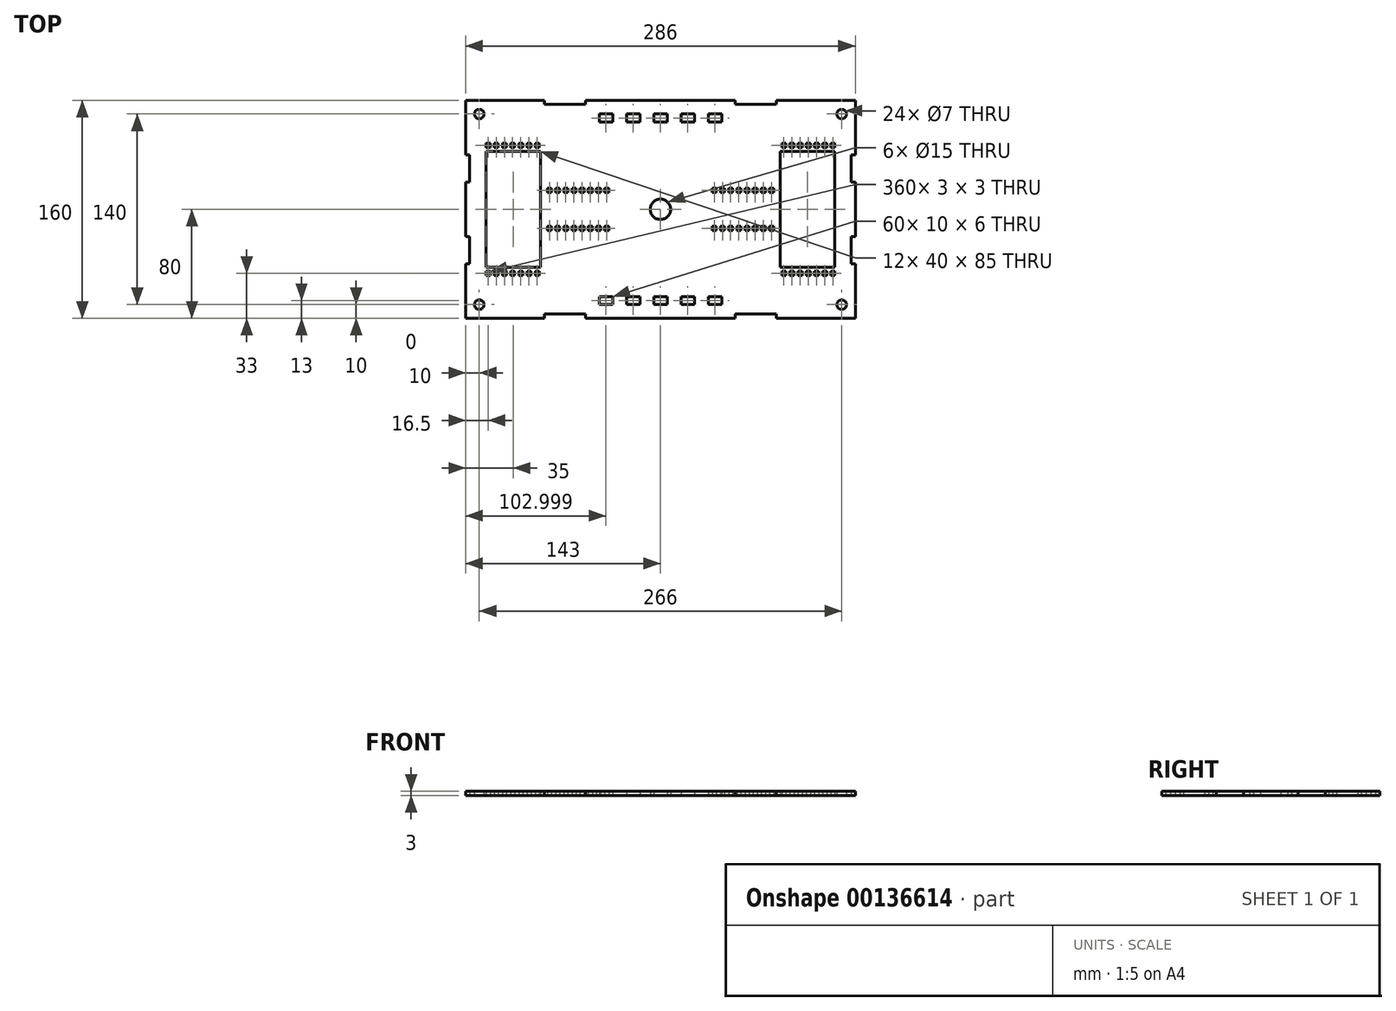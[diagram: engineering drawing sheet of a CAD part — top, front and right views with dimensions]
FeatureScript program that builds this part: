
annotation { "Feature Type Name" : "Feature", "Feature Type Description" : "" }
export const myFeature = defineFeature(function(context is Context, id is Id, definition is map)
    precondition{}
    {
        {
            var Q0;
            Q0=qCreatedBy(makeId("Top.planeOp"),FACE);
            var sketch = newSketch(context, id + "F0", { "sketchPlane" : qUnion([Q0])});
            skLineSegment(sketch, "E0.bottom", {"start": v(143, 80) * mm, "end": v(85, 80) * mm});
            skLineSegment(sketch, "E0.top", {"start": v(143, -80) * mm, "end": v(85, -80) * mm});
            skLineSegment(sketch, "E0.left", {"start": v(143, 80) * mm, "end": v(143, 40) * mm});
            skLineSegment(sketch, "E0.right", {"start": v(-143, 80) * mm, "end": v(-143, 40) * mm});
            skPoint(sketch, "E0.middle", {"position": v(0, 0) * mm});
            skCircle(sketch, "E1", {"center": v(0, 0) * mm, "radius": 7.5 * mm});
            skLineSegment(sketch, "E2", {"start": v(143, 0) * mm, "end": v(128, 0) * mm, "construction": true});
            skLineSegment(sketch, "E3", {"start": v(-70, 0) * mm, "end": v(-65, 0) * mm, "construction": true});
            skLineSegment(sketch, "E4", {"start": v(-65, 0) * mm, "end": v(-65, 12.5) * mm, "construction": true});
            skLineSegment(sketch, "E5", {"start": v(-65, 0) * mm, "end": v(-65, -12.5) * mm, "construction": true});
            skLineSegment(sketch, "E6", {"start": v(-65, 12.5) * mm, "end": v(-62, 12.5) * mm});
            skLineSegment(sketch, "E7", {"start": v(-62, 12.5) * mm, "end": v(-62, 15.5) * mm});
            skLineSegment(sketch, "E8", {"start": v(-62, 15.5) * mm, "end": v(-65, 15.5) * mm});
            skLineSegment(sketch, "E9", {"start": v(-65, 15.5) * mm, "end": v(-65, 12.5) * mm});
            skLineSegment(sketch, "E10", {"start": v(-62, 12.5) * mm, "end": v(-59, 12.5) * mm, "construction": true});
            skLineSegment(sketch, "E11", {"start": v(-59, 12.5) * mm, "end": v(-56, 12.5) * mm, "construction": true});
            skLineSegment(sketch, "E12", {"start": v(-56, 12.5) * mm, "end": v(-53, 12.5) * mm, "construction": true});
            skLineSegment(sketch, "E13", {"start": v(-53, 12.5) * mm, "end": v(-50, 12.5) * mm, "construction": true});
            skLineSegment(sketch, "E14", {"start": v(-50, 12.5) * mm, "end": v(-47, 12.5) * mm, "construction": true});
            skLineSegment(sketch, "E15", {"start": v(-47, 12.5) * mm, "end": v(-44, 12.5) * mm, "construction": true});
            skLineSegment(sketch, "E16", {"start": v(-44, 12.5) * mm, "end": v(-41, 12.5) * mm, "construction": true});
            skLineSegment(sketch, "E17", {"start": v(-41, 12.5) * mm, "end": v(-38, 12.5) * mm, "construction": true});
            skLineSegment(sketch, "E18.bottom", {"start": v(-59, 12.5) * mm, "end": v(-56, 12.5) * mm});
            skLineSegment(sketch, "E18.top", {"start": v(-59, 15.5) * mm, "end": v(-56, 15.5) * mm});
            skLineSegment(sketch, "E18.left", {"start": v(-59, 12.5) * mm, "end": v(-59, 15.5) * mm});
            skLineSegment(sketch, "E18.right", {"start": v(-56, 12.5) * mm, "end": v(-56, 15.5) * mm});
            skLineSegment(sketch, "E19.bottom", {"start": v(-53, 12.5) * mm, "end": v(-50, 12.5) * mm});
            skLineSegment(sketch, "E19.top", {"start": v(-53, 15.5) * mm, "end": v(-50, 15.5) * mm});
            skLineSegment(sketch, "E19.left", {"start": v(-53, 12.5) * mm, "end": v(-53, 15.5) * mm});
            skLineSegment(sketch, "E19.right", {"start": v(-50, 12.5) * mm, "end": v(-50, 15.5) * mm});
            skLineSegment(sketch, "E20.bottom", {"start": v(-47, 12.5) * mm, "end": v(-44, 12.5) * mm});
            skLineSegment(sketch, "E20.top", {"start": v(-47, 15.5) * mm, "end": v(-44, 15.5) * mm});
            skLineSegment(sketch, "E20.left", {"start": v(-47, 12.5) * mm, "end": v(-47, 15.5) * mm});
            skLineSegment(sketch, "E20.right", {"start": v(-44, 12.5) * mm, "end": v(-44, 15.5) * mm});
            skLineSegment(sketch, "E21.bottom", {"start": v(-41, 12.5) * mm, "end": v(-38, 12.5) * mm});
            skLineSegment(sketch, "E21.top", {"start": v(-41, 15.5) * mm, "end": v(-38, 15.5) * mm});
            skLineSegment(sketch, "E21.left", {"start": v(-41, 12.5) * mm, "end": v(-41, 15.5) * mm});
            skLineSegment(sketch, "E21.right", {"start": v(-38, 12.5) * mm, "end": v(-38, 15.5) * mm});
            skLineSegment(sketch, "E22", {"start": v(-65, 12.5) * mm, "end": v(-68, 12.5) * mm, "construction": true});
            skLineSegment(sketch, "E23", {"start": v(-68, 12.5) * mm, "end": v(-71, 12.5) * mm, "construction": true});
            skLineSegment(sketch, "E24", {"start": v(-71, 12.5) * mm, "end": v(-74, 12.5) * mm, "construction": true});
            skLineSegment(sketch, "E25", {"start": v(-74, 12.5) * mm, "end": v(-77, 12.5) * mm, "construction": true});
            skLineSegment(sketch, "E26", {"start": v(-77, 12.5) * mm, "end": v(-80, 12.5) * mm, "construction": true});
            skLineSegment(sketch, "E27", {"start": v(-80, 12.5) * mm, "end": v(-83, 12.5) * mm, "construction": true});
            skLineSegment(sketch, "E28.bottom", {"start": v(-71, 12.5) * mm, "end": v(-68, 12.5) * mm});
            skLineSegment(sketch, "E28.top", {"start": v(-71, 15.5) * mm, "end": v(-68, 15.5) * mm});
            skLineSegment(sketch, "E28.left", {"start": v(-71, 12.5) * mm, "end": v(-71, 15.5) * mm});
            skLineSegment(sketch, "E28.right", {"start": v(-68, 12.5) * mm, "end": v(-68, 15.5) * mm});
            skLineSegment(sketch, "E29.bottom", {"start": v(-77, 12.5) * mm, "end": v(-74, 12.5) * mm});
            skLineSegment(sketch, "E29.top", {"start": v(-77, 15.5) * mm, "end": v(-74, 15.5) * mm});
            skLineSegment(sketch, "E29.left", {"start": v(-77, 12.5) * mm, "end": v(-77, 15.5) * mm});
            skLineSegment(sketch, "E29.right", {"start": v(-74, 12.5) * mm, "end": v(-74, 15.5) * mm});
            skPoint(sketch, "E30.oppositeSnap0", {"position": v(-75.5, 15.5) * mm});
            skLineSegment(sketch, "E30.bottom", {"start": v(-83, 12.5) * mm, "end": v(-80, 12.5) * mm});
            skLineSegment(sketch, "E30.top", {"start": v(-83, 15.5) * mm, "end": v(-80, 15.5) * mm});
            skLineSegment(sketch, "E30.left", {"start": v(-83, 12.5) * mm, "end": v(-83, 15.5) * mm});
            skLineSegment(sketch, "E30.right", {"start": v(-80, 12.5) * mm, "end": v(-80, 15.5) * mm});
            skLineSegment(sketch, "E31.MirrorCS", {"start": v(-77, -12.5) * mm, "end": v(-74, -12.5) * mm});
            skLineSegment(sketch, "E32.MirrorCS", {"start": v(-71, -12.5) * mm, "end": v(-68, -12.5) * mm});
            skLineSegment(sketch, "E33.MirrorCS", {"start": v(-74, -12.5) * mm, "end": v(-77, -12.5) * mm, "construction": true});
            skLineSegment(sketch, "E34.MirrorCS", {"start": v(-77, -12.5) * mm, "end": v(-80, -12.5) * mm, "construction": true});
            skLineSegment(sketch, "E35.MirrorCS", {"start": v(-65, -12.5) * mm, "end": v(-68, -12.5) * mm, "construction": true});
            skLineSegment(sketch, "E36.MirrorCS", {"start": v(-68, -12.5) * mm, "end": v(-71, -12.5) * mm, "construction": true});
            skLineSegment(sketch, "E37.MirrorCS", {"start": v(-83, -12.5) * mm, "end": v(-80, -12.5) * mm});
            skLineSegment(sketch, "E38.MirrorCS", {"start": v(-71, -12.5) * mm, "end": v(-74, -12.5) * mm, "construction": true});
            skLineSegment(sketch, "E39.MirrorCS", {"start": v(-74, -12.5) * mm, "end": v(-74, -15.5) * mm});
            skLineSegment(sketch, "E40.MirrorCS", {"start": v(-80, -12.5) * mm, "end": v(-83, -12.5) * mm, "construction": true});
            skLineSegment(sketch, "E41.MirrorCS", {"start": v(-83, -12.5) * mm, "end": v(-83, -15.5) * mm});
            skLineSegment(sketch, "E42.MirrorCS", {"start": v(-71, -12.5) * mm, "end": v(-71, -15.5) * mm});
            skLineSegment(sketch, "E43.MirrorCS", {"start": v(-83, -15.5) * mm, "end": v(-80, -15.5) * mm});
            skLineSegment(sketch, "E44.MirrorCS", {"start": v(-77, -12.5) * mm, "end": v(-77, -15.5) * mm});
            skLineSegment(sketch, "E45.MirrorCS", {"start": v(-80, -12.5) * mm, "end": v(-80, -15.5) * mm});
            skLineSegment(sketch, "E46.MirrorCS", {"start": v(-68, -12.5) * mm, "end": v(-68, -15.5) * mm});
            skLineSegment(sketch, "E47.MirrorCS", {"start": v(-71, -15.5) * mm, "end": v(-68, -15.5) * mm});
            skLineSegment(sketch, "E48.MirrorCS", {"start": v(-77, -15.5) * mm, "end": v(-74, -15.5) * mm});
            skPoint(sketch, "E49.MirrorP", {"position": v(-70.5, -15.5) * mm});
            skLineSegment(sketch, "E50", {"start": v(-83, 12.5) * mm, "end": v(-83, -12.5) * mm, "construction": true});
            skLineSegment(sketch, "E51", {"start": v(-83, 0) * mm, "end": v(-88, 0) * mm, "construction": true});
            skLineSegment(sketch, "E52", {"start": v(-88, 0) * mm, "end": v(-108, 0) * mm, "construction": true});
            skLineSegment(sketch, "E53.bottom", {"start": v(-88, 42.5) * mm, "end": v(-128, 42.5) * mm});
            skLineSegment(sketch, "E53.top", {"start": v(-88, -42.5) * mm, "end": v(-128, -42.5) * mm});
            skLineSegment(sketch, "E53.left", {"start": v(-88, 42.5) * mm, "end": v(-88, -42.5) * mm});
            skLineSegment(sketch, "E53.right", {"start": v(-128, 42.5) * mm, "end": v(-128, -42.5) * mm});
            skPoint(sketch, "E53.middle", {"position": v(-108, 0) * mm});
            skLineSegment(sketch, "E54", {"start": v(0, 80) * mm, "end": v(0, 70) * mm, "construction": true});
            skLineSegment(sketch, "E55", {"start": v(-128, 42.5) * mm, "end": v(-128, 45.5) * mm, "construction": true});
            skLineSegment(sketch, "E56", {"start": v(-128, 45.5) * mm, "end": v(-125, 45.5) * mm, "construction": true});
            skLineSegment(sketch, "E57", {"start": v(-125, 45.5) * mm, "end": v(-122, 45.5) * mm, "construction": true});
            skPoint(sketch, "E57.endSnap0", {"position": v(-126.5, 45.5) * mm});
            skLineSegment(sketch, "E58", {"start": v(-122, 45.5) * mm, "end": v(-119, 45.5) * mm, "construction": true});
            skLineSegment(sketch, "E59", {"start": v(-119, 45.5) * mm, "end": v(-116, 45.5) * mm, "construction": true});
            skLineSegment(sketch, "E60", {"start": v(-116, 45.5) * mm, "end": v(-113, 45.5) * mm, "construction": true});
            skLineSegment(sketch, "E61", {"start": v(-113, 45.5) * mm, "end": v(-110, 45.5) * mm, "construction": true});
            skLineSegment(sketch, "E62", {"start": v(-110, 45.5) * mm, "end": v(-107, 45.5) * mm, "construction": true});
            skLineSegment(sketch, "E63", {"start": v(-107, 45.5) * mm, "end": v(-104, 45.5) * mm, "construction": true});
            skLineSegment(sketch, "E64", {"start": v(-104, 45.5) * mm, "end": v(-101, 45.5) * mm, "construction": true});
            skLineSegment(sketch, "E65", {"start": v(-101, 45.5) * mm, "end": v(-98, 45.5) * mm, "construction": true});
            skLineSegment(sketch, "E66", {"start": v(-98, 45.5) * mm, "end": v(-95, 45.5) * mm, "construction": true});
            skLineSegment(sketch, "E67", {"start": v(-95, 45.5) * mm, "end": v(-92, 45.5) * mm, "construction": true});
            skLineSegment(sketch, "E68", {"start": v(-92, 45.5) * mm, "end": v(-89, 45.5) * mm, "construction": true});
            skLineSegment(sketch, "E69.bottom", {"start": v(-128, 45.5) * mm, "end": v(-125, 45.5) * mm});
            skLineSegment(sketch, "E69.top", {"start": v(-128, 48.5) * mm, "end": v(-125, 48.5) * mm});
            skLineSegment(sketch, "E69.left", {"start": v(-128, 45.5) * mm, "end": v(-128, 48.5) * mm});
            skLineSegment(sketch, "E69.right", {"start": v(-125, 45.5) * mm, "end": v(-125, 48.5) * mm});
            skLineSegment(sketch, "E70.bottom", {"start": v(-122, 45.5) * mm, "end": v(-119, 45.5) * mm});
            skLineSegment(sketch, "E70.top", {"start": v(-122, 48.5) * mm, "end": v(-119, 48.5) * mm});
            skLineSegment(sketch, "E70.left", {"start": v(-122, 45.5) * mm, "end": v(-122, 48.5) * mm});
            skLineSegment(sketch, "E70.right", {"start": v(-119, 45.5) * mm, "end": v(-119, 48.5) * mm});
            skLineSegment(sketch, "E71.bottom", {"start": v(-116, 45.5) * mm, "end": v(-113, 45.5) * mm});
            skLineSegment(sketch, "E71.top", {"start": v(-116, 48.5) * mm, "end": v(-113, 48.5) * mm});
            skLineSegment(sketch, "E71.left", {"start": v(-116, 45.5) * mm, "end": v(-116, 48.5) * mm});
            skLineSegment(sketch, "E71.right", {"start": v(-113, 45.5) * mm, "end": v(-113, 48.5) * mm});
            skLineSegment(sketch, "E72.bottom", {"start": v(-110, 45.5) * mm, "end": v(-107, 45.5) * mm});
            skLineSegment(sketch, "E72.top", {"start": v(-110, 48.5) * mm, "end": v(-107, 48.5) * mm});
            skLineSegment(sketch, "E72.left", {"start": v(-110, 45.5) * mm, "end": v(-110, 48.5) * mm});
            skLineSegment(sketch, "E72.right", {"start": v(-107, 45.5) * mm, "end": v(-107, 48.5) * mm});
            skLineSegment(sketch, "E73.bottom", {"start": v(-104, 45.5) * mm, "end": v(-101, 45.5) * mm});
            skLineSegment(sketch, "E73.top", {"start": v(-104, 48.5) * mm, "end": v(-101, 48.5) * mm});
            skLineSegment(sketch, "E73.left", {"start": v(-104, 45.5) * mm, "end": v(-104, 48.5) * mm});
            skLineSegment(sketch, "E73.right", {"start": v(-101, 45.5) * mm, "end": v(-101, 48.5) * mm});
            skLineSegment(sketch, "E74.bottom", {"start": v(-98, 45.5) * mm, "end": v(-95, 45.5) * mm});
            skLineSegment(sketch, "E74.top", {"start": v(-98, 48.5) * mm, "end": v(-95, 48.5) * mm});
            skLineSegment(sketch, "E74.left", {"start": v(-98, 45.5) * mm, "end": v(-98, 48.5) * mm});
            skLineSegment(sketch, "E74.right", {"start": v(-95, 45.5) * mm, "end": v(-95, 48.5) * mm});
            skLineSegment(sketch, "E75.bottom", {"start": v(-92, 45.5) * mm, "end": v(-89, 45.5) * mm});
            skLineSegment(sketch, "E75.top", {"start": v(-92, 48.5) * mm, "end": v(-89, 48.5) * mm});
            skLineSegment(sketch, "E75.left", {"start": v(-92, 45.5) * mm, "end": v(-92, 48.5) * mm});
            skLineSegment(sketch, "E75.right", {"start": v(-89, 45.5) * mm, "end": v(-89, 48.5) * mm});
            skLineSegment(sketch, "E76", {"start": v(-143, -80) * mm, "end": v(-133, -80) * mm, "construction": true});
            skLineSegment(sketch, "E77", {"start": v(-133, -80) * mm, "end": v(-133, -70) * mm, "construction": true});
            skCircle(sketch, "E78", {"center": v(-133, -70) * mm, "radius": 3.5 * mm});
            skCircle(sketch, "E79.MirrorC", {"center": v(133, -70) * mm, "radius": 3.5 * mm});
            skCircle(sketch, "E80.MirrorC", {"center": v(133, 70) * mm, "radius": 3.5 * mm});
            skCircle(sketch, "E81.MirrorC", {"center": v(-133, 70) * mm, "radius": 3.5 * mm});
            skLineSegment(sketch, "E82", {"start": v(0, -70) * mm, "end": v(45, -70) * mm, "construction": true});
            skLineSegment(sketch, "E83", {"start": v(0, -70) * mm, "end": v(-22.5, -70) * mm, "construction": true});
            skLineSegment(sketch, "E84", {"start": v(-45, -70) * mm, "end": v(-45, -64) * mm});
            skLineSegment(sketch, "E85", {"start": v(-45, -64) * mm, "end": v(-35, -64) * mm});
            skLineSegment(sketch, "E86", {"start": v(-35, -64) * mm, "end": v(-35, -70) * mm});
            skLineSegment(sketch, "E87", {"start": v(-35, -70) * mm, "end": v(-45, -70) * mm});
            skLineSegment(sketch, "E88.trimOffspring", {"start": v(-35, -70) * mm, "end": v(-45, -70) * mm, "construction": true});
            skLineSegment(sketch, "E89", {"start": v(-35, -70) * mm, "end": v(-25, -70) * mm, "construction": true});
            skLineSegment(sketch, "E90", {"start": v(-25, -70) * mm, "end": v(-11.25, -70) * mm, "construction": true});
            skLineSegment(sketch, "E91", {"start": v(-25, -70) * mm, "end": v(-15, -70) * mm, "construction": true});
            skLineSegment(sketch, "E92", {"start": v(-15, -70) * mm, "end": v(-5, -70) * mm, "construction": true});
            skLineSegment(sketch, "E93", {"start": v(-5, -70) * mm, "end": v(5, -70) * mm, "construction": true});
            skLineSegment(sketch, "E94", {"start": v(5, -70) * mm, "end": v(15, -70) * mm, "construction": true});
            skLineSegment(sketch, "E95", {"start": v(15, -70) * mm, "end": v(25, -70) * mm, "construction": true});
            skLineSegment(sketch, "E96", {"start": v(25, -70) * mm, "end": v(35, -70) * mm, "construction": true});
            skLineSegment(sketch, "E97.bottom", {"start": v(-25, -70) * mm, "end": v(-15, -70) * mm});
            skLineSegment(sketch, "E97.top", {"start": v(-25, -64) * mm, "end": v(-15, -64) * mm});
            skLineSegment(sketch, "E97.left", {"start": v(-25, -70) * mm, "end": v(-25, -64) * mm});
            skLineSegment(sketch, "E97.right", {"start": v(-15, -70) * mm, "end": v(-15, -64) * mm});
            skLineSegment(sketch, "E98.bottom", {"start": v(-5, -70) * mm, "end": v(5, -70) * mm});
            skLineSegment(sketch, "E98.top", {"start": v(-5, -64) * mm, "end": v(5, -64) * mm});
            skLineSegment(sketch, "E98.left", {"start": v(-5, -70) * mm, "end": v(-5, -64) * mm});
            skLineSegment(sketch, "E98.right", {"start": v(5, -70) * mm, "end": v(5, -64) * mm});
            skLineSegment(sketch, "E99.bottom", {"start": v(15, -70) * mm, "end": v(25, -70) * mm});
            skLineSegment(sketch, "E99.top", {"start": v(15, -64) * mm, "end": v(25, -64) * mm});
            skLineSegment(sketch, "E99.left", {"start": v(15, -70) * mm, "end": v(15, -64) * mm});
            skLineSegment(sketch, "E99.right", {"start": v(25, -70) * mm, "end": v(25, -64) * mm});
            skLineSegment(sketch, "E100.bottom", {"start": v(35, -70) * mm, "end": v(45, -70) * mm});
            skLineSegment(sketch, "E100.top", {"start": v(35, -64) * mm, "end": v(45, -64) * mm});
            skLineSegment(sketch, "E100.left", {"start": v(35, -70) * mm, "end": v(35, -64) * mm});
            skLineSegment(sketch, "E100.right", {"start": v(45, -70) * mm, "end": v(45, -64) * mm});
            skLineSegment(sketch, "E101.MirrorCS", {"start": v(77, 12.5) * mm, "end": v(74, 12.5) * mm});
            skLineSegment(sketch, "E102.MirrorCS", {"start": v(71, -12.5) * mm, "end": v(68, -12.5) * mm});
            skLineSegment(sketch, "E103.MirrorCS", {"start": v(71, 12.5) * mm, "end": v(71, 15.5) * mm});
            skLineSegment(sketch, "E104.MirrorCS", {"start": v(77, 15.5) * mm, "end": v(74, 15.5) * mm});
            skLineSegment(sketch, "E105.MirrorCS", {"start": v(77, 12.5) * mm, "end": v(77, 15.5) * mm});
            skLineSegment(sketch, "E106.MirrorCS", {"start": v(74, 12.5) * mm, "end": v(74, 15.5) * mm});
            skLineSegment(sketch, "E107.MirrorCS", {"start": v(71, 12.5) * mm, "end": v(74, 12.5) * mm, "construction": true});
            skLineSegment(sketch, "E108.MirrorCS", {"start": v(83, -12.5) * mm, "end": v(80, -12.5) * mm});
            skLineSegment(sketch, "E109.MirrorCS", {"start": v(74, 12.5) * mm, "end": v(77, 12.5) * mm, "construction": true});
            skLineSegment(sketch, "E110.MirrorCS", {"start": v(53, 12.5) * mm, "end": v(50, 12.5) * mm});
            skLineSegment(sketch, "E111.MirrorCS", {"start": v(53, 15.5) * mm, "end": v(50, 15.5) * mm});
            skLineSegment(sketch, "E112.MirrorCS", {"start": v(80, -12.5) * mm, "end": v(80, -15.5) * mm});
            skLineSegment(sketch, "E113.MirrorCS", {"start": v(47, 12.5) * mm, "end": v(44, 12.5) * mm});
            skLineSegment(sketch, "E114.MirrorCS", {"start": v(68, 12.5) * mm, "end": v(68, 15.5) * mm});
            skLineSegment(sketch, "E115.MirrorCS", {"start": v(77, -12.5) * mm, "end": v(80, -12.5) * mm, "construction": true});
            skLineSegment(sketch, "E116.MirrorCS", {"start": v(71, 12.5) * mm, "end": v(68, 12.5) * mm});
            skLineSegment(sketch, "E117.MirrorCS", {"start": v(53, 12.5) * mm, "end": v(53, 15.5) * mm});
            skLineSegment(sketch, "E118.MirrorCS", {"start": v(53, 12.5) * mm, "end": v(50, 12.5) * mm, "construction": true});
            skLineSegment(sketch, "E119.MirrorCS", {"start": v(80, -12.5) * mm, "end": v(83, -12.5) * mm, "construction": true});
            skLineSegment(sketch, "E120.MirrorCS", {"start": v(41, 12.5) * mm, "end": v(38, 12.5) * mm});
            skLineSegment(sketch, "E121.MirrorCS", {"start": v(83, -12.5) * mm, "end": v(83, -15.5) * mm});
            skLineSegment(sketch, "E122.MirrorCS", {"start": v(50, 12.5) * mm, "end": v(50, 15.5) * mm});
            skLineSegment(sketch, "E123.MirrorCS", {"start": v(71, -12.5) * mm, "end": v(71, -15.5) * mm});
            skLineSegment(sketch, "E124.MirrorCS", {"start": v(68, -12.5) * mm, "end": v(71, -12.5) * mm, "construction": true});
            skLineSegment(sketch, "E125.MirrorCS", {"start": v(77, -12.5) * mm, "end": v(74, -12.5) * mm});
            skLineSegment(sketch, "E126.MirrorCS", {"start": v(59, 12.5) * mm, "end": v(56, 12.5) * mm});
            skLineSegment(sketch, "E127.MirrorCS", {"start": v(65, 12.5) * mm, "end": v(68, 12.5) * mm, "construction": true});
            skLineSegment(sketch, "E128.MirrorCS", {"start": v(62, 12.5) * mm, "end": v(59, 12.5) * mm, "construction": true});
            skLineSegment(sketch, "E129.MirrorCS", {"start": v(56, 12.5) * mm, "end": v(53, 12.5) * mm, "construction": true});
            skLineSegment(sketch, "E130.MirrorCS", {"start": v(65, 12.5) * mm, "end": v(62, 12.5) * mm});
            skLineSegment(sketch, "E131.MirrorCS", {"start": v(62, 12.5) * mm, "end": v(62, 15.5) * mm});
            skLineSegment(sketch, "E132.MirrorCS", {"start": v(62, 15.5) * mm, "end": v(65, 15.5) * mm});
            skLineSegment(sketch, "E133.MirrorCS", {"start": v(65, 15.5) * mm, "end": v(65, 12.5) * mm});
            skLineSegment(sketch, "E134.MirrorCS", {"start": v(59, 12.5) * mm, "end": v(59, 15.5) * mm});
            skLineSegment(sketch, "E135.MirrorCS", {"start": v(71, -12.5) * mm, "end": v(74, -12.5) * mm, "construction": true});
            skLineSegment(sketch, "E136.MirrorCS", {"start": v(74, -12.5) * mm, "end": v(74, -15.5) * mm});
            skLineSegment(sketch, "E137.MirrorCS", {"start": v(47, 15.5) * mm, "end": v(44, 15.5) * mm});
            skLineSegment(sketch, "E138.MirrorCS", {"start": v(47, 12.5) * mm, "end": v(47, 15.5) * mm});
            skLineSegment(sketch, "E139.MirrorCS", {"start": v(68, -12.5) * mm, "end": v(68, -15.5) * mm});
            skLineSegment(sketch, "E140.MirrorCS", {"start": v(44, 12.5) * mm, "end": v(44, 15.5) * mm});
            skLineSegment(sketch, "E141.MirrorCS", {"start": v(50, 12.5) * mm, "end": v(47, 12.5) * mm, "construction": true});
            skLineSegment(sketch, "E142.MirrorCS", {"start": v(65, -12.5) * mm, "end": v(68, -12.5) * mm, "construction": true});
            skLineSegment(sketch, "E143.MirrorCS", {"start": v(47, 12.5) * mm, "end": v(44, 12.5) * mm, "construction": true});
            skLineSegment(sketch, "E144.MirrorCS", {"start": v(74, -12.5) * mm, "end": v(77, -12.5) * mm, "construction": true});
            skLineSegment(sketch, "E145.MirrorCS", {"start": v(71, 15.5) * mm, "end": v(68, 15.5) * mm});
            skLineSegment(sketch, "E146.MirrorCS", {"start": v(41, 15.5) * mm, "end": v(38, 15.5) * mm});
            skLineSegment(sketch, "E147.MirrorCS", {"start": v(44, 12.5) * mm, "end": v(41, 12.5) * mm, "construction": true});
            skLineSegment(sketch, "E148.MirrorCS", {"start": v(83, 12.5) * mm, "end": v(80, 12.5) * mm});
            skLineSegment(sketch, "E149.MirrorCS", {"start": v(41, 12.5) * mm, "end": v(41, 15.5) * mm});
            skLineSegment(sketch, "E150.MirrorCS", {"start": v(41, 12.5) * mm, "end": v(38, 12.5) * mm, "construction": true});
            skLineSegment(sketch, "E151.MirrorCS", {"start": v(77, 12.5) * mm, "end": v(80, 12.5) * mm, "construction": true});
            skLineSegment(sketch, "E152.MirrorCS", {"start": v(59, 12.5) * mm, "end": v(56, 12.5) * mm, "construction": true});
            skLineSegment(sketch, "E153.MirrorCS", {"start": v(59, 15.5) * mm, "end": v(56, 15.5) * mm});
            skLineSegment(sketch, "E154.MirrorCS", {"start": v(68, 12.5) * mm, "end": v(71, 12.5) * mm, "construction": true});
            skLineSegment(sketch, "E155.MirrorCS", {"start": v(77, -12.5) * mm, "end": v(77, -15.5) * mm});
            skLineSegment(sketch, "E156.MirrorCS", {"start": v(56, 12.5) * mm, "end": v(56, 15.5) * mm});
            skLineSegment(sketch, "E157.MirrorCS", {"start": v(80, 12.5) * mm, "end": v(83, 12.5) * mm, "construction": true});
            skLineSegment(sketch, "E158.MirrorCS", {"start": v(83, 15.5) * mm, "end": v(80, 15.5) * mm});
            skLineSegment(sketch, "E159.MirrorCS", {"start": v(83, 12.5) * mm, "end": v(83, 15.5) * mm});
            skLineSegment(sketch, "E160.MirrorCS", {"start": v(80, 12.5) * mm, "end": v(80, 15.5) * mm});
            skLineSegment(sketch, "E161.MirrorCS", {"start": v(77, -15.5) * mm, "end": v(74, -15.5) * mm});
            skLineSegment(sketch, "E162.MirrorCS", {"start": v(38, 12.5) * mm, "end": v(38, 15.5) * mm});
            skLineSegment(sketch, "E163.MirrorCS", {"start": v(71, -15.5) * mm, "end": v(68, -15.5) * mm});
            skLineSegment(sketch, "E164.MirrorCS", {"start": v(83, -15.5) * mm, "end": v(80, -15.5) * mm});
            skLineSegment(sketch, "E165.MirrorCS", {"start": v(70, 0) * mm, "end": v(65, 0) * mm, "construction": true});
            skLineSegment(sketch, "E166.MirrorCS", {"start": v(65, 0) * mm, "end": v(65, 12.5) * mm, "construction": true});
            skLineSegment(sketch, "E167.MirrorCS", {"start": v(83, 0) * mm, "end": v(88, 0) * mm, "construction": true});
            skPoint(sketch, "E168.MirrorP", {"position": v(75.5, 15.5) * mm});
            skPoint(sketch, "E169.MirrorP", {"position": v(70.5, -15.5) * mm});
            skLineSegment(sketch, "E170.MirrorCS", {"start": v(83, 12.5) * mm, "end": v(83, -12.5) * mm, "construction": true});
            skLineSegment(sketch, "E171.MirrorCS", {"start": v(65, 0) * mm, "end": v(65, -12.5) * mm, "construction": true});
            skLineSegment(sketch, "E172.MirrorCS", {"start": v(104, 45.5) * mm, "end": v(101, 45.5) * mm});
            skLineSegment(sketch, "E173.MirrorCS", {"start": v(110, 45.5) * mm, "end": v(107, 45.5) * mm});
            skLineSegment(sketch, "E174.MirrorCS", {"start": v(98, 45.5) * mm, "end": v(98, 48.5) * mm});
            skLineSegment(sketch, "E175.MirrorCS", {"start": v(104, 45.5) * mm, "end": v(101, 45.5) * mm, "construction": true});
            skLineSegment(sketch, "E176.MirrorCS", {"start": v(113, 45.5) * mm, "end": v(113, 48.5) * mm});
            skLineSegment(sketch, "E177.MirrorCS", {"start": v(98, 48.5) * mm, "end": v(95, 48.5) * mm});
            skLineSegment(sketch, "E178.MirrorCS", {"start": v(98, 45.5) * mm, "end": v(95, 45.5) * mm});
            skLineSegment(sketch, "E179.MirrorCS", {"start": v(101, 45.5) * mm, "end": v(101, 48.5) * mm});
            skLineSegment(sketch, "E180.MirrorCS", {"start": v(104, 45.5) * mm, "end": v(104, 48.5) * mm});
            skLineSegment(sketch, "E181.MirrorCS", {"start": v(107, 45.5) * mm, "end": v(104, 45.5) * mm, "construction": true});
            skLineSegment(sketch, "E182.MirrorCS", {"start": v(104, 48.5) * mm, "end": v(101, 48.5) * mm});
            skLineSegment(sketch, "E183.MirrorCS", {"start": v(113, 45.5) * mm, "end": v(110, 45.5) * mm, "construction": true});
            skLineSegment(sketch, "E184.MirrorCS", {"start": v(128, 45.5) * mm, "end": v(125, 45.5) * mm});
            skLineSegment(sketch, "E185.MirrorCS", {"start": v(110, 45.5) * mm, "end": v(107, 45.5) * mm, "construction": true});
            skLineSegment(sketch, "E186.MirrorCS", {"start": v(107, 45.5) * mm, "end": v(107, 48.5) * mm});
            skLineSegment(sketch, "E187.MirrorCS", {"start": v(110, 45.5) * mm, "end": v(110, 48.5) * mm});
            skLineSegment(sketch, "E188.MirrorCS", {"start": v(110, 48.5) * mm, "end": v(107, 48.5) * mm});
            skLineSegment(sketch, "E189.MirrorCS", {"start": v(101, 45.5) * mm, "end": v(98, 45.5) * mm, "construction": true});
            skLineSegment(sketch, "E190.MirrorCS", {"start": v(125, 45.5) * mm, "end": v(122, 45.5) * mm, "construction": true});
            skLineSegment(sketch, "E191.MirrorCS", {"start": v(122, 45.5) * mm, "end": v(119, 45.5) * mm});
            skLineSegment(sketch, "E192.MirrorCS", {"start": v(125, 45.5) * mm, "end": v(125, 48.5) * mm});
            skLineSegment(sketch, "E193.MirrorCS", {"start": v(128, 45.5) * mm, "end": v(125, 45.5) * mm, "construction": true});
            skLineSegment(sketch, "E194.MirrorCS", {"start": v(128, 45.5) * mm, "end": v(128, 48.5) * mm});
            skLineSegment(sketch, "E195.MirrorCS", {"start": v(128, 42.5) * mm, "end": v(128, 45.5) * mm, "construction": true});
            skLineSegment(sketch, "E196.MirrorCS", {"start": v(92, 45.5) * mm, "end": v(92, 48.5) * mm});
            skLineSegment(sketch, "E197.MirrorCS", {"start": v(128, 48.5) * mm, "end": v(125, 48.5) * mm});
            skLineSegment(sketch, "E198.MirrorCS", {"start": v(116, 45.5) * mm, "end": v(113, 45.5) * mm});
            skLineSegment(sketch, "E199.MirrorCS", {"start": v(95, 45.5) * mm, "end": v(92, 45.5) * mm, "construction": true});
            skLineSegment(sketch, "E200.MirrorCS", {"start": v(98, 45.5) * mm, "end": v(95, 45.5) * mm, "construction": true});
            skLineSegment(sketch, "E201.MirrorCS", {"start": v(95, 45.5) * mm, "end": v(95, 48.5) * mm});
            skLineSegment(sketch, "E202.MirrorCS", {"start": v(119, 45.5) * mm, "end": v(116, 45.5) * mm, "construction": true});
            skLineSegment(sketch, "E203.MirrorCS", {"start": v(122, 45.5) * mm, "end": v(122, 48.5) * mm});
            skLineSegment(sketch, "E204.MirrorCS", {"start": v(122, 48.5) * mm, "end": v(119, 48.5) * mm});
            skLineSegment(sketch, "E205.MirrorCS", {"start": v(122, 45.5) * mm, "end": v(119, 45.5) * mm, "construction": true});
            skLineSegment(sketch, "E206.MirrorCS", {"start": v(116, 45.5) * mm, "end": v(116, 48.5) * mm});
            skLineSegment(sketch, "E207.MirrorCS", {"start": v(92, 45.5) * mm, "end": v(89, 45.5) * mm});
            skLineSegment(sketch, "E208.MirrorCS", {"start": v(116, 48.5) * mm, "end": v(113, 48.5) * mm});
            skLineSegment(sketch, "E209.MirrorCS", {"start": v(116, 45.5) * mm, "end": v(113, 45.5) * mm, "construction": true});
            skLineSegment(sketch, "E210.MirrorCS", {"start": v(119, 45.5) * mm, "end": v(119, 48.5) * mm});
            skLineSegment(sketch, "E211.MirrorCS", {"start": v(89, 45.5) * mm, "end": v(89, 48.5) * mm});
            skLineSegment(sketch, "E212.MirrorCS", {"start": v(88, -42.5) * mm, "end": v(128, -42.5) * mm});
            skLineSegment(sketch, "E213.MirrorCS", {"start": v(88, 42.5) * mm, "end": v(128, 42.5) * mm});
            skLineSegment(sketch, "E214.MirrorCS", {"start": v(92, 45.5) * mm, "end": v(89, 45.5) * mm, "construction": true});
            skLineSegment(sketch, "E215.MirrorCS", {"start": v(92, 48.5) * mm, "end": v(89, 48.5) * mm});
            skLineSegment(sketch, "E216.MirrorCS", {"start": v(123, -42.5) * mm, "end": v(123, -45.5) * mm, "construction": true});
            skPoint(sketch, "E217.MirrorP", {"position": v(126.5, 45.5) * mm});
            skLineSegment(sketch, "E218.MirrorCS", {"start": v(88, 42.5) * mm, "end": v(88, -42.5) * mm});
            skLineSegment(sketch, "E219.MirrorCS", {"start": v(88, 0) * mm, "end": v(108, 0) * mm, "construction": true});
            skPoint(sketch, "E220.MirrorP", {"position": v(108, 0) * mm});
            skLineSegment(sketch, "E221.MirrorCS", {"start": v(128, 42.5) * mm, "end": v(128, -42.5) * mm});
            skLineSegment(sketch, "E222.MirrorCS", {"start": v(-47, -12.5) * mm, "end": v(-44, -12.5) * mm});
            skLineSegment(sketch, "E223.MirrorCS", {"start": v(-50, -12.5) * mm, "end": v(-47, -12.5) * mm, "construction": true});
            skLineSegment(sketch, "E224.MirrorCS", {"start": v(-41, -12.5) * mm, "end": v(-38, -12.5) * mm});
            skLineSegment(sketch, "E225.MirrorCS", {"start": v(-47, -12.5) * mm, "end": v(-44, -12.5) * mm, "construction": true});
            skLineSegment(sketch, "E226.MirrorCS", {"start": v(-56, -12.5) * mm, "end": v(-53, -12.5) * mm, "construction": true});
            skLineSegment(sketch, "E227.MirrorCS", {"start": v(-41, -12.5) * mm, "end": v(-38, -12.5) * mm, "construction": true});
            skLineSegment(sketch, "E228.MirrorCS", {"start": v(-62, -12.5) * mm, "end": v(-59, -12.5) * mm, "construction": true});
            skLineSegment(sketch, "E229.MirrorCS", {"start": v(-65, -12.5) * mm, "end": v(-62, -12.5) * mm});
            skLineSegment(sketch, "E230.MirrorCS", {"start": v(-47, -15.5) * mm, "end": v(-44, -15.5) * mm});
            skLineSegment(sketch, "E231.MirrorCS", {"start": v(-41, -15.5) * mm, "end": v(-38, -15.5) * mm});
            skLineSegment(sketch, "E232.MirrorCS", {"start": v(-62, -15.5) * mm, "end": v(-65, -15.5) * mm});
            skLineSegment(sketch, "E233.MirrorCS", {"start": v(-53, -12.5) * mm, "end": v(-50, -12.5) * mm});
            skLineSegment(sketch, "E234.MirrorCS", {"start": v(-53, -12.5) * mm, "end": v(-50, -12.5) * mm, "construction": true});
            skLineSegment(sketch, "E235.MirrorCS", {"start": v(-44, -12.5) * mm, "end": v(-44, -15.5) * mm});
            skLineSegment(sketch, "E236.MirrorCS", {"start": v(-41, -12.5) * mm, "end": v(-41, -15.5) * mm});
            skLineSegment(sketch, "E237.MirrorCS", {"start": v(-53, -15.5) * mm, "end": v(-50, -15.5) * mm});
            skLineSegment(sketch, "E238.MirrorCS", {"start": v(-38, -12.5) * mm, "end": v(-38, -15.5) * mm});
            skLineSegment(sketch, "E239.MirrorCS", {"start": v(-59, -12.5) * mm, "end": v(-56, -12.5) * mm});
            skLineSegment(sketch, "E240.MirrorCS", {"start": v(-59, -15.5) * mm, "end": v(-56, -15.5) * mm});
            skLineSegment(sketch, "E241.MirrorCS", {"start": v(-47, -12.5) * mm, "end": v(-47, -15.5) * mm});
            skLineSegment(sketch, "E242.MirrorCS", {"start": v(-53, -12.5) * mm, "end": v(-53, -15.5) * mm});
            skLineSegment(sketch, "E243.MirrorCS", {"start": v(-59, -12.5) * mm, "end": v(-59, -15.5) * mm});
            skLineSegment(sketch, "E244.MirrorCS", {"start": v(-56, -12.5) * mm, "end": v(-56, -15.5) * mm});
            skLineSegment(sketch, "E245.MirrorCS", {"start": v(-50, -12.5) * mm, "end": v(-50, -15.5) * mm});
            skLineSegment(sketch, "E246.MirrorCS", {"start": v(-62, -12.5) * mm, "end": v(-62, -15.5) * mm});
            skLineSegment(sketch, "E247.MirrorCS", {"start": v(-65, -15.5) * mm, "end": v(-65, -12.5) * mm});
            skLineSegment(sketch, "E248.MirrorCS", {"start": v(-44, -12.5) * mm, "end": v(-41, -12.5) * mm, "construction": true});
            skLineSegment(sketch, "E249.MirrorCS", {"start": v(-59, -12.5) * mm, "end": v(-56, -12.5) * mm, "construction": true});
            skLineSegment(sketch, "E250.MirrorCS", {"start": v(47, -12.5) * mm, "end": v(44, -12.5) * mm});
            skLineSegment(sketch, "E251.MirrorCS", {"start": v(53, -12.5) * mm, "end": v(50, -12.5) * mm});
            skLineSegment(sketch, "E252.MirrorCS", {"start": v(59, -12.5) * mm, "end": v(56, -12.5) * mm});
            skLineSegment(sketch, "E253.MirrorCS", {"start": v(47, -12.5) * mm, "end": v(44, -12.5) * mm, "construction": true});
            skLineSegment(sketch, "E254.MirrorCS", {"start": v(44, -12.5) * mm, "end": v(41, -12.5) * mm, "construction": true});
            skLineSegment(sketch, "E255.MirrorCS", {"start": v(53, -12.5) * mm, "end": v(50, -12.5) * mm, "construction": true});
            skLineSegment(sketch, "E256.MirrorCS", {"start": v(56, -12.5) * mm, "end": v(53, -12.5) * mm, "construction": true});
            skLineSegment(sketch, "E257.MirrorCS", {"start": v(41, -12.5) * mm, "end": v(38, -12.5) * mm});
            skLineSegment(sketch, "E258.MirrorCS", {"start": v(59, -12.5) * mm, "end": v(56, -12.5) * mm, "construction": true});
            skLineSegment(sketch, "E259.MirrorCS", {"start": v(50, -12.5) * mm, "end": v(47, -12.5) * mm, "construction": true});
            skLineSegment(sketch, "E260.MirrorCS", {"start": v(65, -12.5) * mm, "end": v(62, -12.5) * mm});
            skLineSegment(sketch, "E261.MirrorCS", {"start": v(41, -12.5) * mm, "end": v(38, -12.5) * mm, "construction": true});
            skLineSegment(sketch, "E262.MirrorCS", {"start": v(62, -12.5) * mm, "end": v(59, -12.5) * mm, "construction": true});
            skLineSegment(sketch, "E263.MirrorCS", {"start": v(50, -12.5) * mm, "end": v(50, -15.5) * mm});
            skLineSegment(sketch, "E264.MirrorCS", {"start": v(38, -12.5) * mm, "end": v(38, -15.5) * mm});
            skLineSegment(sketch, "E265.MirrorCS", {"start": v(41, -15.5) * mm, "end": v(38, -15.5) * mm});
            skLineSegment(sketch, "E266.MirrorCS", {"start": v(62, -12.5) * mm, "end": v(62, -15.5) * mm});
            skLineSegment(sketch, "E267.MirrorCS", {"start": v(47, -15.5) * mm, "end": v(44, -15.5) * mm});
            skLineSegment(sketch, "E268.MirrorCS", {"start": v(62, -15.5) * mm, "end": v(65, -15.5) * mm});
            skLineSegment(sketch, "E269.MirrorCS", {"start": v(59, -15.5) * mm, "end": v(56, -15.5) * mm});
            skLineSegment(sketch, "E270.MirrorCS", {"start": v(41, -12.5) * mm, "end": v(41, -15.5) * mm});
            skLineSegment(sketch, "E271.MirrorCS", {"start": v(65, -15.5) * mm, "end": v(65, -12.5) * mm});
            skLineSegment(sketch, "E272.MirrorCS", {"start": v(53, -12.5) * mm, "end": v(53, -15.5) * mm});
            skLineSegment(sketch, "E273.MirrorCS", {"start": v(59, -12.5) * mm, "end": v(59, -15.5) * mm});
            skLineSegment(sketch, "E274.MirrorCS", {"start": v(44, -12.5) * mm, "end": v(44, -15.5) * mm});
            skLineSegment(sketch, "E275.MirrorCS", {"start": v(56, -12.5) * mm, "end": v(56, -15.5) * mm});
            skLineSegment(sketch, "E276.MirrorCS", {"start": v(53, -15.5) * mm, "end": v(50, -15.5) * mm});
            skLineSegment(sketch, "E277.MirrorCS", {"start": v(47, -12.5) * mm, "end": v(47, -15.5) * mm});
            skLineSegment(sketch, "E278.MirrorCS", {"start": v(128, -45.5) * mm, "end": v(125, -45.5) * mm});
            skLineSegment(sketch, "E279.MirrorCS", {"start": v(98, -45.5) * mm, "end": v(95, -45.5) * mm});
            skLineSegment(sketch, "E280.MirrorCS", {"start": v(128, -45.5) * mm, "end": v(125, -45.5) * mm, "construction": true});
            skLineSegment(sketch, "E281.MirrorCS", {"start": v(122, -45.5) * mm, "end": v(119, -45.5) * mm});
            skLineSegment(sketch, "E282.MirrorCS", {"start": v(92, -45.5) * mm, "end": v(89, -45.5) * mm});
            skLineSegment(sketch, "E283.MirrorCS", {"start": v(110, -45.5) * mm, "end": v(107, -45.5) * mm});
            skLineSegment(sketch, "E284.MirrorCS", {"start": v(104, -45.5) * mm, "end": v(101, -45.5) * mm});
            skLineSegment(sketch, "E285.MirrorCS", {"start": v(116, -45.5) * mm, "end": v(113, -45.5) * mm});
            skLineSegment(sketch, "E286.MirrorCS", {"start": v(101, -45.5) * mm, "end": v(101, -48.5) * mm});
            skLineSegment(sketch, "E287.MirrorCS", {"start": v(89, -45.5) * mm, "end": v(89, -48.5) * mm});
            skLineSegment(sketch, "E288.MirrorCS", {"start": v(128, -48.5) * mm, "end": v(125, -48.5) * mm});
            skLineSegment(sketch, "E289.MirrorCS", {"start": v(107, -45.5) * mm, "end": v(104, -45.5) * mm, "construction": true});
            skLineSegment(sketch, "E290.MirrorCS", {"start": v(110, -45.5) * mm, "end": v(110, -48.5) * mm});
            skLineSegment(sketch, "E291.MirrorCS", {"start": v(128, -45.5) * mm, "end": v(128, -48.5) * mm});
            skLineSegment(sketch, "E292.MirrorCS", {"start": v(122, -45.5) * mm, "end": v(122, -48.5) * mm});
            skLineSegment(sketch, "E293.MirrorCS", {"start": v(119, -45.5) * mm, "end": v(119, -48.5) * mm});
            skLineSegment(sketch, "E294.MirrorCS", {"start": v(98, -48.5) * mm, "end": v(95, -48.5) * mm});
            skLineSegment(sketch, "E295.MirrorCS", {"start": v(116, -45.5) * mm, "end": v(113, -45.5) * mm, "construction": true});
            skLineSegment(sketch, "E296.MirrorCS", {"start": v(125, -45.5) * mm, "end": v(125, -48.5) * mm});
            skLineSegment(sketch, "E297.MirrorCS", {"start": v(113, -45.5) * mm, "end": v(113, -48.5) * mm});
            skLineSegment(sketch, "E298.MirrorCS", {"start": v(116, -48.5) * mm, "end": v(113, -48.5) * mm});
            skLineSegment(sketch, "E299.MirrorCS", {"start": v(110, -45.5) * mm, "end": v(107, -45.5) * mm, "construction": true});
            skLineSegment(sketch, "E300.MirrorCS", {"start": v(107, -45.5) * mm, "end": v(107, -48.5) * mm});
            skLineSegment(sketch, "E301.MirrorCS", {"start": v(95, -45.5) * mm, "end": v(95, -48.5) * mm});
            skLineSegment(sketch, "E302.MirrorCS", {"start": v(119, -45.5) * mm, "end": v(116, -45.5) * mm, "construction": true});
            skLineSegment(sketch, "E303.MirrorCS", {"start": v(104, -45.5) * mm, "end": v(101, -45.5) * mm, "construction": true});
            skLineSegment(sketch, "E304.MirrorCS", {"start": v(92, -45.5) * mm, "end": v(92, -48.5) * mm});
            skPoint(sketch, "E305.MirrorP", {"position": v(126.5, -45.5) * mm});
            skLineSegment(sketch, "E306.MirrorCS", {"start": v(104, -48.5) * mm, "end": v(101, -48.5) * mm});
            skLineSegment(sketch, "E307.MirrorCS", {"start": v(104, -45.5) * mm, "end": v(104, -48.5) * mm});
            skLineSegment(sketch, "E308.MirrorCS", {"start": v(98, -45.5) * mm, "end": v(98, -48.5) * mm});
            skLineSegment(sketch, "E309.MirrorCS", {"start": v(125, -45.5) * mm, "end": v(122, -45.5) * mm, "construction": true});
            skLineSegment(sketch, "E310.MirrorCS", {"start": v(116, -45.5) * mm, "end": v(116, -48.5) * mm});
            skLineSegment(sketch, "E311.MirrorCS", {"start": v(101, -45.5) * mm, "end": v(98, -45.5) * mm, "construction": true});
            skLineSegment(sketch, "E312.MirrorCS", {"start": v(122, -45.5) * mm, "end": v(119, -45.5) * mm, "construction": true});
            skLineSegment(sketch, "E313.MirrorCS", {"start": v(110, -48.5) * mm, "end": v(107, -48.5) * mm});
            skLineSegment(sketch, "E314.MirrorCS", {"start": v(122, -48.5) * mm, "end": v(119, -48.5) * mm});
            skLineSegment(sketch, "E315.MirrorCS", {"start": v(92, -45.5) * mm, "end": v(89, -45.5) * mm, "construction": true});
            skLineSegment(sketch, "E316.MirrorCS", {"start": v(98, -45.5) * mm, "end": v(95, -45.5) * mm, "construction": true});
            skLineSegment(sketch, "E317.MirrorCS", {"start": v(113, -45.5) * mm, "end": v(110, -45.5) * mm, "construction": true});
            skLineSegment(sketch, "E318.MirrorCS", {"start": v(92, -48.5) * mm, "end": v(89, -48.5) * mm});
            skLineSegment(sketch, "E319.MirrorCS", {"start": v(95, -45.5) * mm, "end": v(92, -45.5) * mm, "construction": true});
            skLineSegment(sketch, "E320.MirrorCS", {"start": v(-128, -45.5) * mm, "end": v(-125, -45.5) * mm});
            skLineSegment(sketch, "E321.MirrorCS", {"start": v(-110, -45.5) * mm, "end": v(-107, -45.5) * mm});
            skLineSegment(sketch, "E322.MirrorCS", {"start": v(-116, -45.5) * mm, "end": v(-113, -45.5) * mm});
            skLineSegment(sketch, "E323.MirrorCS", {"start": v(-128, -45.5) * mm, "end": v(-125, -45.5) * mm, "construction": true});
            skLineSegment(sketch, "E324.MirrorCS", {"start": v(-104, -45.5) * mm, "end": v(-101, -45.5) * mm});
            skLineSegment(sketch, "E325.MirrorCS", {"start": v(-98, -45.5) * mm, "end": v(-95, -45.5) * mm});
            skLineSegment(sketch, "E326.MirrorCS", {"start": v(-122, -45.5) * mm, "end": v(-119, -45.5) * mm});
            skLineSegment(sketch, "E327.MirrorCS", {"start": v(-92, -45.5) * mm, "end": v(-89, -45.5) * mm});
            skLineSegment(sketch, "E328.MirrorCS", {"start": v(-128, -48.5) * mm, "end": v(-125, -48.5) * mm});
            skLineSegment(sketch, "E329.MirrorCS", {"start": v(-107, -45.5) * mm, "end": v(-104, -45.5) * mm, "construction": true});
            skLineSegment(sketch, "E330.MirrorCS", {"start": v(-116, -45.5) * mm, "end": v(-116, -48.5) * mm});
            skLineSegment(sketch, "E331.MirrorCS", {"start": v(-95, -45.5) * mm, "end": v(-95, -48.5) * mm});
            skLineSegment(sketch, "E332.MirrorCS", {"start": v(-92, -45.5) * mm, "end": v(-92, -48.5) * mm});
            skPoint(sketch, "E333.MirrorP", {"position": v(-126.5, -45.5) * mm});
            skLineSegment(sketch, "E334.MirrorCS", {"start": v(-104, -45.5) * mm, "end": v(-101, -45.5) * mm, "construction": true});
            skLineSegment(sketch, "E335.MirrorCS", {"start": v(-113, -45.5) * mm, "end": v(-113, -48.5) * mm});
            skLineSegment(sketch, "E336.MirrorCS", {"start": v(-89, -45.5) * mm, "end": v(-89, -48.5) * mm});
            skLineSegment(sketch, "E337.MirrorCS", {"start": v(-101, -45.5) * mm, "end": v(-98, -45.5) * mm, "construction": true});
            skLineSegment(sketch, "E338.MirrorCS", {"start": v(-98, -48.5) * mm, "end": v(-95, -48.5) * mm});
            skLineSegment(sketch, "E339.MirrorCS", {"start": v(-128, -42.5) * mm, "end": v(-128, -45.5) * mm, "construction": true});
            skLineSegment(sketch, "E340.MirrorCS", {"start": v(-104, -45.5) * mm, "end": v(-104, -48.5) * mm});
            skLineSegment(sketch, "E341.MirrorCS", {"start": v(-110, -48.5) * mm, "end": v(-107, -48.5) * mm});
            skLineSegment(sketch, "E342.MirrorCS", {"start": v(-92, -48.5) * mm, "end": v(-89, -48.5) * mm});
            skLineSegment(sketch, "E343.MirrorCS", {"start": v(-98, -45.5) * mm, "end": v(-95, -45.5) * mm, "construction": true});
            skLineSegment(sketch, "E344.MirrorCS", {"start": v(-128, -45.5) * mm, "end": v(-128, -48.5) * mm});
            skLineSegment(sketch, "E345.MirrorCS", {"start": v(-125, -45.5) * mm, "end": v(-122, -45.5) * mm, "construction": true});
            skLineSegment(sketch, "E346.MirrorCS", {"start": v(-113, -45.5) * mm, "end": v(-110, -45.5) * mm, "construction": true});
            skLineSegment(sketch, "E347.MirrorCS", {"start": v(-110, -45.5) * mm, "end": v(-110, -48.5) * mm});
            skLineSegment(sketch, "E348.MirrorCS", {"start": v(-95, -45.5) * mm, "end": v(-92, -45.5) * mm, "construction": true});
            skLineSegment(sketch, "E349.MirrorCS", {"start": v(-107, -45.5) * mm, "end": v(-107, -48.5) * mm});
            skLineSegment(sketch, "E350.MirrorCS", {"start": v(-92, -45.5) * mm, "end": v(-89, -45.5) * mm, "construction": true});
            skLineSegment(sketch, "E351.MirrorCS", {"start": v(-116, -48.5) * mm, "end": v(-113, -48.5) * mm});
            skLineSegment(sketch, "E352.MirrorCS", {"start": v(-110, -45.5) * mm, "end": v(-107, -45.5) * mm, "construction": true});
            skLineSegment(sketch, "E353.MirrorCS", {"start": v(-101, -45.5) * mm, "end": v(-101, -48.5) * mm});
            skLineSegment(sketch, "E354.MirrorCS", {"start": v(-125, -45.5) * mm, "end": v(-125, -48.5) * mm});
            skLineSegment(sketch, "E355.MirrorCS", {"start": v(-122, -45.5) * mm, "end": v(-119, -45.5) * mm, "construction": true});
            skLineSegment(sketch, "E356.MirrorCS", {"start": v(-122, -48.5) * mm, "end": v(-119, -48.5) * mm});
            skLineSegment(sketch, "E357.MirrorCS", {"start": v(-122, -45.5) * mm, "end": v(-122, -48.5) * mm});
            skLineSegment(sketch, "E358.MirrorCS", {"start": v(-119, -45.5) * mm, "end": v(-116, -45.5) * mm, "construction": true});
            skLineSegment(sketch, "E359.MirrorCS", {"start": v(-116, -45.5) * mm, "end": v(-113, -45.5) * mm, "construction": true});
            skLineSegment(sketch, "E360.MirrorCS", {"start": v(-119, -45.5) * mm, "end": v(-119, -48.5) * mm});
            skLineSegment(sketch, "E361.MirrorCS", {"start": v(-104, -48.5) * mm, "end": v(-101, -48.5) * mm});
            skLineSegment(sketch, "E362.MirrorCS", {"start": v(-98, -45.5) * mm, "end": v(-98, -48.5) * mm});
            skLineSegment(sketch, "E363", {"start": v(0, -80) * mm, "end": v(55, -80) * mm});
            skLineSegment(sketch, "E364", {"start": v(55, -80) * mm, "end": v(55, -77) * mm});
            skLineSegment(sketch, "E365", {"start": v(55, -77) * mm, "end": v(85, -77) * mm});
            skLineSegment(sketch, "E366", {"start": v(85, -77) * mm, "end": v(85, -80) * mm});
            skLineSegment(sketch, "E367.trimOffspring", {"start": v(55, -80) * mm, "end": v(-55, -80) * mm});
            skLineSegment(sketch, "E368", {"start": v(0, -80) * mm, "end": v(-55, -80) * mm, "construction": true});
            skLineSegment(sketch, "E369", {"start": v(-55, -80) * mm, "end": v(-55, -77) * mm});
            skLineSegment(sketch, "E370", {"start": v(-55, -77) * mm, "end": v(-85, -77) * mm});
            skLineSegment(sketch, "E371", {"start": v(-85, -77) * mm, "end": v(-85, -80) * mm});
            skLineSegment(sketch, "E372.trimOffspring", {"start": v(-85, -80) * mm, "end": v(-143, -80) * mm});
            skLineSegment(sketch, "E373", {"start": v(143, 0) * mm, "end": v(143, -20) * mm, "construction": true});
            skLineSegment(sketch, "E374", {"start": v(143, -20) * mm, "end": v(143, 20) * mm, "construction": true});
            skLineSegment(sketch, "E375", {"start": v(143, -20) * mm, "end": v(140, -20) * mm});
            skLineSegment(sketch, "E376", {"start": v(140, -20) * mm, "end": v(140, -40) * mm});
            skLineSegment(sketch, "E377", {"start": v(140, -40) * mm, "end": v(143, -40) * mm});
            skLineSegment(sketch, "E378.trimOffspring", {"start": v(143, -40) * mm, "end": v(143, -80) * mm});
            skLineSegment(sketch, "E379", {"start": v(143, 20) * mm, "end": v(140, 20) * mm});
            skLineSegment(sketch, "E380", {"start": v(140, 20) * mm, "end": v(140, 40) * mm});
            skLineSegment(sketch, "E381", {"start": v(140, 40) * mm, "end": v(143, 40) * mm});
            skLineSegment(sketch, "E382.trimOffspring", {"start": v(143, 20) * mm, "end": v(143, -20) * mm});
            skLineSegment(sketch, "E383", {"start": v(0, 80) * mm, "end": v(0, -80) * mm, "construction": true});
            skLineSegment(sketch, "E384", {"start": v(-143, 0) * mm, "end": v(143, 0) * mm, "construction": true});
            skLineSegment(sketch, "E385.MirrorCS", {"start": v(-55, 77) * mm, "end": v(-85, 77) * mm});
            skLineSegment(sketch, "E386.MirrorCS", {"start": v(-85, 77) * mm, "end": v(-85, 80) * mm});
            skLineSegment(sketch, "E387.MirrorCS", {"start": v(-55, 80) * mm, "end": v(-55, 77) * mm});
            skLineSegment(sketch, "E388.MirrorCS", {"start": v(55, 77) * mm, "end": v(85, 77) * mm});
            skLineSegment(sketch, "E389.MirrorCS", {"start": v(55, 80) * mm, "end": v(55, 77) * mm});
            skLineSegment(sketch, "E390.MirrorCS", {"start": v(85, 77) * mm, "end": v(85, 80) * mm});
            skLineSegment(sketch, "E391.MirrorCS", {"start": v(-140, 40) * mm, "end": v(-143, 40) * mm});
            skLineSegment(sketch, "E392.MirrorCS", {"start": v(-140, 20) * mm, "end": v(-140, 40) * mm});
            skLineSegment(sketch, "E393.MirrorCS", {"start": v(-143, 20) * mm, "end": v(-140, 20) * mm});
            skLineSegment(sketch, "E394.MirrorCS", {"start": v(-143, -20) * mm, "end": v(-140, -20) * mm});
            skLineSegment(sketch, "E395.MirrorCS", {"start": v(-140, -20) * mm, "end": v(-140, -40) * mm});
            skLineSegment(sketch, "E396.MirrorCS", {"start": v(-140, -40) * mm, "end": v(-143, -40) * mm});
            skLineSegment(sketch, "E397.trimOffspring", {"start": v(-143, 20) * mm, "end": v(-143, -20) * mm});
            skLineSegment(sketch, "E398.trimOffspring", {"start": v(-143, -40) * mm, "end": v(-143, -80) * mm});
            skLineSegment(sketch, "E399.trimOffspring", {"start": v(-85, 80) * mm, "end": v(-143, 80) * mm});
            skLineSegment(sketch, "E400.trimOffspring", {"start": v(55, 80) * mm, "end": v(-55, 80) * mm});
            skLineSegment(sketch, "E401.MirrorCS", {"start": v(-25, 70) * mm, "end": v(-15, 70) * mm});
            skLineSegment(sketch, "E402.MirrorCS", {"start": v(-5, 70) * mm, "end": v(5, 70) * mm});
            skLineSegment(sketch, "E403.MirrorCS", {"start": v(35, 70) * mm, "end": v(35, 64) * mm});
            skLineSegment(sketch, "E404.MirrorCS", {"start": v(45, 70) * mm, "end": v(45, 64) * mm});
            skLineSegment(sketch, "E405.MirrorCS", {"start": v(-25, 70) * mm, "end": v(-25, 64) * mm});
            skLineSegment(sketch, "E406.MirrorCS", {"start": v(0, 70) * mm, "end": v(-22.5, 70) * mm, "construction": true});
            skLineSegment(sketch, "E407.MirrorCS", {"start": v(-15, 70) * mm, "end": v(-15, 64) * mm});
            skLineSegment(sketch, "E408.MirrorCS", {"start": v(-45, 70) * mm, "end": v(-45, 64) * mm});
            skLineSegment(sketch, "E409.MirrorCS", {"start": v(-35, 64) * mm, "end": v(-35, 70) * mm});
            skLineSegment(sketch, "E410.MirrorCS", {"start": v(-5, 70) * mm, "end": v(-5, 64) * mm});
            skLineSegment(sketch, "E411.MirrorCS", {"start": v(5, 70) * mm, "end": v(5, 64) * mm});
            skLineSegment(sketch, "E412.MirrorCS", {"start": v(15, 70) * mm, "end": v(25, 70) * mm});
            skLineSegment(sketch, "E413.MirrorCS", {"start": v(-25, 70) * mm, "end": v(-11.25, 70) * mm, "construction": true});
            skLineSegment(sketch, "E414.MirrorCS", {"start": v(15, 70) * mm, "end": v(15, 64) * mm});
            skLineSegment(sketch, "E415.MirrorCS", {"start": v(25, 70) * mm, "end": v(25, 64) * mm});
            skLineSegment(sketch, "E416.MirrorCS", {"start": v(-5, 70) * mm, "end": v(5, 70) * mm, "construction": true});
            skLineSegment(sketch, "E417.MirrorCS", {"start": v(15, 70) * mm, "end": v(25, 70) * mm, "construction": true});
            skLineSegment(sketch, "E418.MirrorCS", {"start": v(25, 70) * mm, "end": v(35, 70) * mm, "construction": true});
            skLineSegment(sketch, "E419.MirrorCS", {"start": v(-35, 70) * mm, "end": v(-45, 70) * mm});
            skLineSegment(sketch, "E420.MirrorCS", {"start": v(-35, 70) * mm, "end": v(-25, 70) * mm, "construction": true});
            skLineSegment(sketch, "E421.MirrorCS", {"start": v(5, 70) * mm, "end": v(15, 70) * mm, "construction": true});
            skLineSegment(sketch, "E422.MirrorCS", {"start": v(15, 64) * mm, "end": v(25, 64) * mm});
            skLineSegment(sketch, "E423.MirrorCS", {"start": v(-25, 70) * mm, "end": v(-15, 70) * mm, "construction": true});
            skLineSegment(sketch, "E424.MirrorCS", {"start": v(-15, 70) * mm, "end": v(-5, 70) * mm, "construction": true});
            skLineSegment(sketch, "E425.MirrorCS", {"start": v(35, 70) * mm, "end": v(45, 70) * mm});
            skLineSegment(sketch, "E426.MirrorCS", {"start": v(0, 70) * mm, "end": v(45, 70) * mm, "construction": true});
            skLineSegment(sketch, "E427.MirrorCS", {"start": v(-25, 64) * mm, "end": v(-15, 64) * mm});
            skLineSegment(sketch, "E428.MirrorCS", {"start": v(-45, 64) * mm, "end": v(-35, 64) * mm});
            skLineSegment(sketch, "E429.MirrorCS", {"start": v(-5, 64) * mm, "end": v(5, 64) * mm});
            skLineSegment(sketch, "E430.MirrorCS", {"start": v(-35, 70) * mm, "end": v(-45, 70) * mm, "construction": true});
            skLineSegment(sketch, "E431.MirrorCS", {"start": v(35, 64) * mm, "end": v(45, 64) * mm});
            skSolve(sketch);
        }
        {
            var Q0;
            Q0=makeQuery(id+"F0.imprint","IMPRINT",FACE,{"disambiguationData":[TD([[makeQuery(id+"F0.imprint","IMPRINT",EDGE,{"derivedFrom":sQuery(id+"F0.wireOp",EDGE,"E0.bottom")}),1.0]])]});
            extrude(context, id + "F1", {"entities" : qUnion([Q0]), "endBound" : BoundingType.SYMMETRIC, "depth" : 3 * mm});
        }
    });
